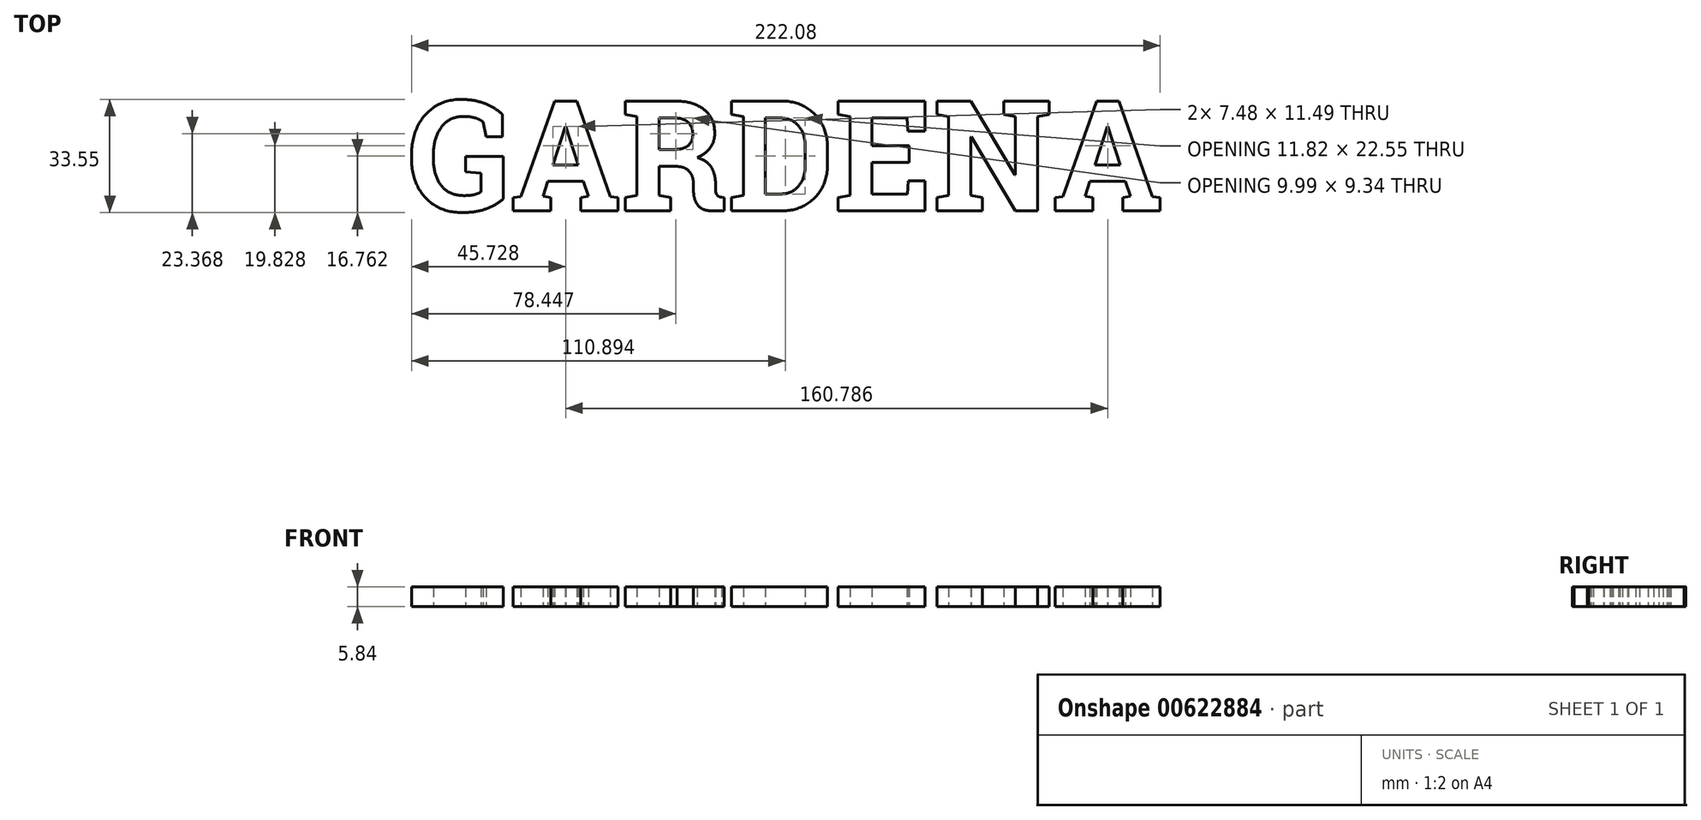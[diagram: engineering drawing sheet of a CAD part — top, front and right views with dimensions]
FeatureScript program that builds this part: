
annotation { "Feature Type Name" : "Feature", "Feature Type Description" : "" }
export const myFeature = defineFeature(function(context is Context, id is Id, definition is map)
    precondition{}
    {
        {
            var Q0;
            Q0=qCreatedBy(makeId("Top.planeOp"),FACE);
            var sketch = newSketch(context, id + "F0", { "sketchPlane" : qUnion([Q0])});
            skText(sketch, "E0", { "text": "GARDENA", "fontName": "RobotoSlab-Bold.ttf"});
            const initialGuessF0  = {"E0": [-0.06298, -0.01384, 1, 0, 0.03302]};
            skSetInitialGuess(sketch, initialGuessF0);
            skSolve(sketch);
        }
        {
            var Q0;
            Q0 = qSketchRegion(id + "F0", true);
            extrude(context, id + "F1", {"entities" : qUnion([Q0]), "depth" : 5.84 * mm, "offsetDistance" : 25.4 * mm});
        }
    });
